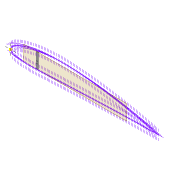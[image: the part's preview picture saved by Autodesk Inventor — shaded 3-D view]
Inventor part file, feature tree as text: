
AUTODESK INVENTOR PART (.ipt)
format: ipt  version: 2022 (Build 260153000, 153)  size: 434,176 bytes
history: native  units: mm
features: sketch x8, projected_geometry x8, extrude x7, shell x1, plane x1, chamfer x1
ambient origin geometry x8: Origin, YZ Plane, XZ Plane, XY Plane, X Axis, Y Axis, Z Axis, Center Point
bodies: Solid1 (feature_tree)
feature tree (26):
  extrude  "Extrusion1"  Depth=2.0mm
  shell  "Shell1"  Thickness=2.0mm
  extrude  "Extrusion8"  Depth=2.0mm
  extrude  "Extrusion3"  Depth=10.0mm TaperAngle=0.0deg
  extrude  "Extrusion4"  Depth=5.0mm
  extrude  "Extrusion5"  Depth=2.5mm
  plane  "Work Plane2"
  extrude  "Extrusion9"  Depth=5.0mm
  chamfer  "Chamfer1"  Distance=5.0mm
  extrude  "Extrusion11"  Depth=2.0mm TaperAngle=0.0deg
  sketch  "Sketch30"  dims[d40=2.5mm]
  sketch  "Sketch31"  dims[d62=72.0mm d63=5.0mm d64=2.0mm d65=0.0mm d66=2.5mm d67=12.0mm d68=75.0mm d69=20.0mm d70=0.5mm d71=10.0mm d72=0.0mm d75=3.0mm d76=3.0mm d77=2.0mm d78=45.0deg d79=0.0mm d80=1.0mm d81=1.0mm d82=1.0mm d83=1.0mm d84=1.0mm d85=10.0mm d86=0.0mm]
  sketch  "Sketch3"  dims[d0=2.0mm d1=0.0mm d2=4.0mm d7=2.0mm]
  sketch  "Sketch8"  dims[d8=2.0mm d9=5.9mm]
  sketch  "Sketch9"  dims[d13=10.0mm d14=0.0mm d16=10.0mm d17=0.0mm]
  projected_geometry  "Projected Loop4"
  projected_geometry  "Projected Loop10"
  sketch  "Sketch24"  dims[d22=2.0mm d23=0.0mm d32=5.0mm]
  projected_geometry  "Projected Loop11"
  projected_geometry  "Projected Loop12"
  sketch  "Sketch26"  dims[d34=1.6mm d35=2.5mm]
  projected_geometry  "Projected Loop13"
  sketch  "Sketch29"  dims[d37=5.0mm d38=1.6mm]
  projected_geometry  "Project Cut Edges1"
  projected_geometry  "Project Cut Edges2"
  projected_geometry  "Project Cut Edges3"
